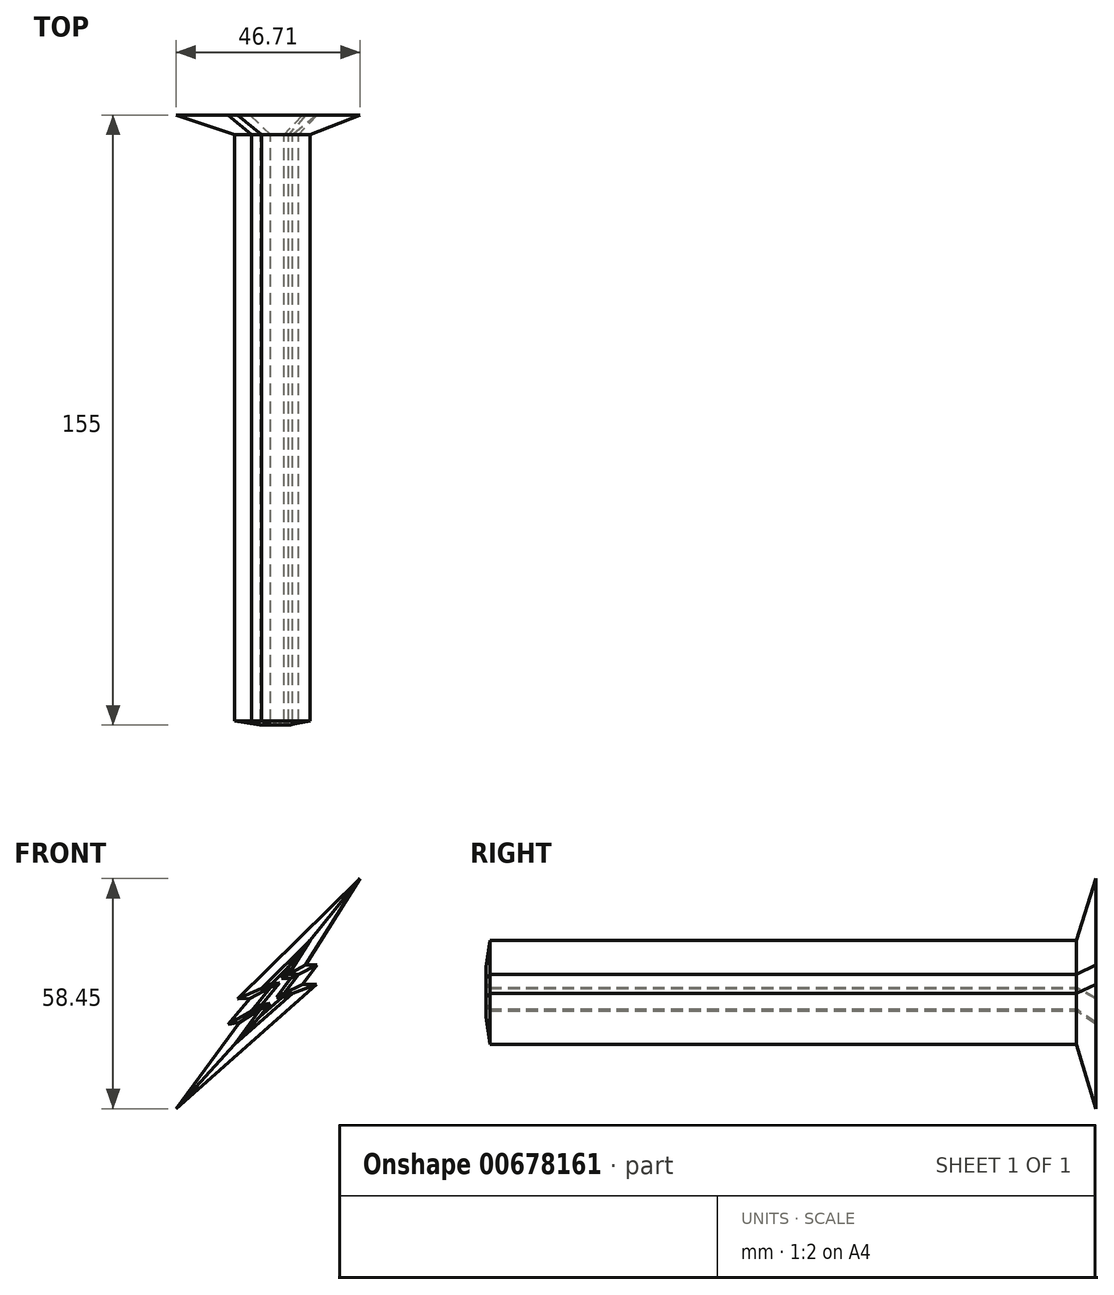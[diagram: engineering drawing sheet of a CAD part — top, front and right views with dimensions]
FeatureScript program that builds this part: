
annotation { "Feature Type Name" : "Feature", "Feature Type Description" : "" }
export const myFeature = defineFeature(function(context is Context, id is Id, definition is map)
    precondition{}
    {
        {
            var Q0;
            Q0=qCreatedBy(makeId("Front.planeOp"),FACE);
            var sketch = newSketch(context, id + "F0", { "sketchPlane" : qUnion([Q0])});
            skLineSegment(sketch, "E0", {"start": v(-5.58, -3.06) * mm, "end": v(6.78, 9.07) * mm});
            skLineSegment(sketch, "E1", {"start": v(6.78, 9.07) * mm, "end": v(1.35, 0.47) * mm});
            skLineSegment(sketch, "E2", {"start": v(1.35, 0.47) * mm, "end": v(3.84, 0.47) * mm});
            skLineSegment(sketch, "E3", {"start": v(3.84, 0.47) * mm, "end": v(0.2, -4.4) * mm});
            skLineSegment(sketch, "E4", {"start": v(2.26, -4.4) * mm, "end": v(-12.42, -17.4) * mm});
            skLineSegment(sketch, "E5", {"start": v(-12.42, -17.4) * mm, "end": v(-5.78, -8.36) * mm});
            skLineSegment(sketch, "E6", {"start": v(-5.78, -8.36) * mm, "end": v(-8.14, -8.81) * mm});
            skLineSegment(sketch, "E7", {"start": v(-8.14, -8.81) * mm, "end": v(-3.26, -2.9) * mm});
            skLineSegment(sketch, "E8", {"start": v(-3.26, -2.9) * mm, "end": v(-5.58, -3.06) * mm});
            skLineSegment(sketch, "E9", {"start": v(0.2, -4.4) * mm, "end": v(2.26, -4.4) * mm});
            skSolve(sketch);
        }
        {
            var Q0;
            Q0=makeQuery(id+"F0.imprint","IMPRINT",FACE,{"disambiguationData":[TD([[makeQuery(id+"F0.imprint","IMPRINT",EDGE,{"derivedFrom":sQuery(id+"F0.wireOp",EDGE,"E0")}),-1.0]])]});
            extrude(context, id + "F1", {"entities" : qUnion([Q0]), "depth" : 150 * mm, "offsetDistance" : 25 * mm});
        }
        {
            var Q0;
            Q0=makeQuery(id+"F1.opExtrude","CAP_FACE",FACE,{"disambiguationData":[OSD([sQuery(id+"F0.wireOp",EDGE,"E0"),sQuery(id+"F0.wireOp",EDGE,"E1"),sQuery(id+"F0.wireOp",EDGE,"E2"),sQuery(id+"F0.wireOp",EDGE,"E3"),sQuery(id+"F0.wireOp",EDGE,"E4"),sQuery(id+"F0.wireOp",EDGE,"E5"),sQuery(id+"F0.wireOp",EDGE,"E6"),sQuery(id+"F0.wireOp",EDGE,"E7"),sQuery(id+"F0.wireOp",EDGE,"E8"),sQuery(id+"F0.wireOp",EDGE,"E9")])],"isStart":true});
            extrude(context, id + "F2", {"entities" : qUnion([Q0]), "operationType" : NewBodyOperationType.ADD, "depth" : 5 * mm, "offsetDistance" : 25 * mm, "hasDraft" : true, "draftAngle" : 25 * degree});
        }
        {
            var Q0;
            Q0=makeQuery(id+"F1.opExtrude","CAP_EDGE",EDGE,{"disambiguationData":[OSD([sQuery(id+"F0.wireOp",EDGE,"E4")])],"isStart":false});
            var Q1;
            Q1=makeQuery(id+"F1.opExtrude","CAP_EDGE",EDGE,{"disambiguationData":[OSD([sQuery(id+"F0.wireOp",EDGE,"E3")])],"isStart":false});
            var Q2;
            Q2=makeQuery(id+"F1.opExtrude","CAP_FACE",FACE,{"disambiguationData":[OSD([sQuery(id+"F0.wireOp",EDGE,"E0"),sQuery(id+"F0.wireOp",EDGE,"E1"),sQuery(id+"F0.wireOp",EDGE,"E2"),sQuery(id+"F0.wireOp",EDGE,"E3"),sQuery(id+"F0.wireOp",EDGE,"E4"),sQuery(id+"F0.wireOp",EDGE,"E5"),sQuery(id+"F0.wireOp",EDGE,"E6"),sQuery(id+"F0.wireOp",EDGE,"E7"),sQuery(id+"F0.wireOp",EDGE,"E8"),sQuery(id+"F0.wireOp",EDGE,"E9")])],"isStart":false});
            chamfer(context, id + "F3", {"entities" : qUnion([Q0, Q1, Q2]), "width" : 1 * mm, "tangentPropagation" : true});
        }
    });
